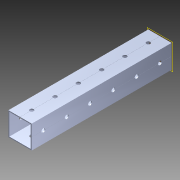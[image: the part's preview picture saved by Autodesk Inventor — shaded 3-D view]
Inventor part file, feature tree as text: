
AUTODESK INVENTOR PART (.ipt)
format: ipt  version: 2014 SP1 (Build 180222100, 222)  size: 1,141,248 bytes
history: native  units: in
note: dims shown in document units (in); Inventor stores cm internally (conversion verified against a paired STEP export)
features: pattern_circular x1, other x1, plane x1, extrude x1, imported_body x1, sketch x1
ambient origin geometry x8: Origin, YZ Plane, XZ Plane, XY Plane, X Axis, Y Axis, Z Axis, Center Point
bodies: Body1 (feature_tree)
feature tree (6):
  pattern_circular  "CirPattern2"
  other  "217-3426-STEP1"
  plane  "Work Plane1"
  extrude  "Extrusion1"  Depth=3937.0079in TaperAngle=0.0deg
  imported_body  "Base1"
  sketch  "Sketch1"  dims[d0=-6.0in d1=3937.0079in d2=0.0in]
